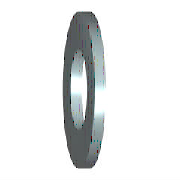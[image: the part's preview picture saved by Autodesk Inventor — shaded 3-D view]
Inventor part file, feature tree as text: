
AUTODESK INVENTOR PART (.ipt)
format: ipt  version: 2021 (Build 250183000, 183)  size: 109,568 bytes
history: native  units: mm (DEFAULTED — no unit token found)
features: other x1, plane x1, sketch x1
ambient origin geometry x7: Origin, YZ Plane, XY Plane, X Axis, Y Axis, Z Axis, Center Point
bodies: Solid1 (feature_tree), Body (feature_tree)
feature tree (3):
  other  "Work Axis1"
  plane  "Work Plane1"
  sketch  "Sketch"  dims[d0=2.8mm d1=5.7mm d2=0.5mm d3=0.0mm d4=0.0mm d5=0.0mm d6=0.0mm d7=0.0mm]
